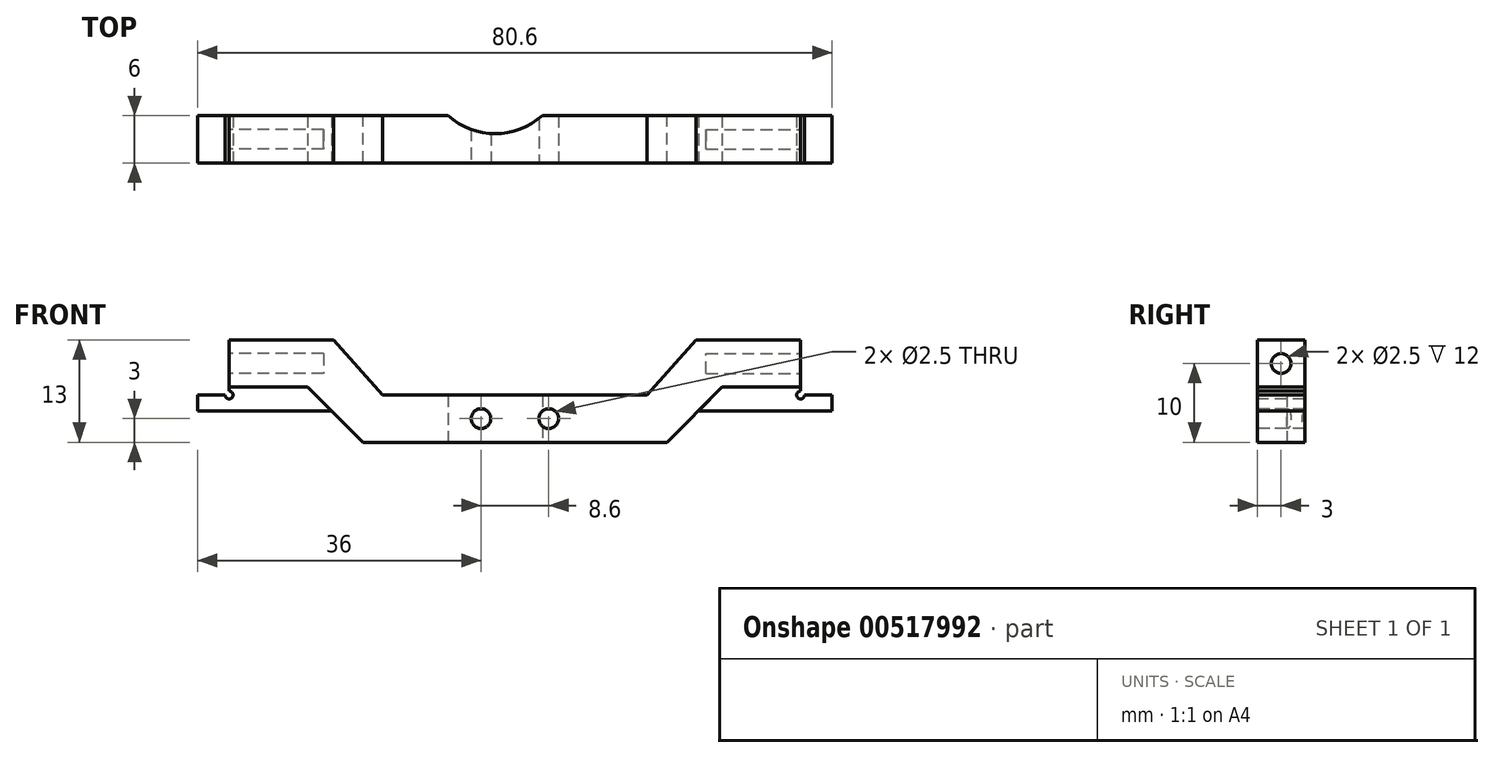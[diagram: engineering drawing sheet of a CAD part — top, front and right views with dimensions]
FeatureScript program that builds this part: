
annotation { "Feature Type Name" : "Feature", "Feature Type Description" : "" }
export const myFeature = defineFeature(function(context is Context, id is Id, definition is map)
    precondition{}
    {
        {
            var Q0;
            Q0=qCreatedBy(makeId("Top.planeOp"),FACE);
            var sketch = newSketch(context, id + "F0", { "sketchPlane" : qUnion([Q0])});
            skLineSegment(sketch, "E0.bottom", {"start": v(-33.8, 3) * mm, "end": v(38.8, 3) * mm});
            skLineSegment(sketch, "E0.top", {"start": v(-33.8, -3) * mm, "end": v(-6, -3) * mm});
            skLineSegment(sketch, "E0.left", {"start": v(-33.8, 3) * mm, "end": v(-33.8, -3) * mm});
            skLineSegment(sketch, "E0.right", {"start": v(38.8, 3) * mm, "end": v(38.8, -3) * mm});
            skLineSegment(sketch, "E1.trimOffspring", {"start": v(6, -3) * mm, "end": v(38.8, -3) * mm});
            skLineSegment(sketch, "E2", {"start": v(-6, -3) * mm, "end": v(6, -3) * mm});
            skSolve(sketch);
        }
        {
            var Q0;
            Q0=makeQuery(id+"F0.imprint","IMPRINT",FACE,{"disambiguationData":[TD([[makeQuery(id+"F0.imprint","IMPRINT",EDGE,{"derivedFrom":sQuery(id+"F0.wireOp",EDGE,"E0.bottom")}),-1.0]])]});
            extrude(context, id + "F1", {"entities" : qUnion([Q0]), "depth" : 13 * mm, "offsetDistance" : 25 * mm});
        }
        {
            var Q0;
            Q0=makeQuery(id+"F1.opExtrude","SWEPT_FACE",FACE,{"disambiguationData":[OSD([sQuery(id+"F0.wireOp",EDGE,"E0.bottom")])]});
            var sketch = newSketch(context, id + "F2", { "sketchPlane" : qUnion([Q0])});
            skLineSegment(sketch, "E3", {"start": v(-38.8, 0) * mm, "end": v(33.8, 0) * mm});
            skLineSegment(sketch, "E4", {"start": v(33.8, 0) * mm, "end": v(33.8, 13) * mm});
            skLineSegment(sketch, "E5", {"start": v(33.8, 13) * mm, "end": v(-38.8, 13) * mm});
            skLineSegment(sketch, "E6", {"start": v(-38.8, 13) * mm, "end": v(-38.8, 0) * mm});
            skLineSegment(sketch, "E7", {"start": v(-38.8, 7) * mm, "end": v(-28.8, 7) * mm});
            skLineSegment(sketch, "E8", {"start": v(-28.8, 7) * mm, "end": v(-28.8, 0) * mm});
            skLineSegment(sketch, "E9", {"start": v(23.8, 7) * mm, "end": v(23.8, 0) * mm});
            skLineSegment(sketch, "E10", {"start": v(-28.8, 7) * mm, "end": v(-21.8, 0) * mm});
            skLineSegment(sketch, "E11", {"start": v(23.8, 7) * mm, "end": v(16.8, 0) * mm});
            skLineSegment(sketch, "E12.trimOffspring", {"start": v(23.8, 7) * mm, "end": v(33.8, 7) * mm});
            skLineSegment(sketch, "E13.0", {"start": v(-24.56, 11.24) * mm, "end": v(-20.28, 6.97) * mm});
            skLineSegment(sketch, "E14.0", {"start": v(19.56, 11.24) * mm, "end": v(14.31, 6) * mm});
            skLineSegment(sketch, "E15", {"start": v(-19.31, 6) * mm, "end": v(14.31, 6) * mm});
            skPoint(sketch, "E15.startSnap0", {"position": v(-20.28, 6.97) * mm});
            skPoint(sketch, "E16.orphan", {"position": v(-27.25, 13.94) * mm});
            skPoint(sketch, "E17.orphan", {"position": v(-19.34, -2.46) * mm});
            skPoint(sketch, "E18.orphan", {"position": v(14.34, -2.46) * mm});
            skPoint(sketch, "E19.orphan", {"position": v(6.71, 0) * mm});
            skLineSegment(sketch, "E20.trimOffspring", {"start": v(-19.31, 6) * mm, "end": v(-25.51, 13) * mm});
            skPoint(sketch, "E21.end.orphan", {"position": v(-13.31, 0) * mm});
            skLineSegment(sketch, "E22.trimOffspring", {"start": v(14.31, 6) * mm, "end": v(20.51, 13) * mm});
            skPoint(sketch, "E23.orphan", {"position": v(-20.28, 6) * mm});
            skSolve(sketch);
        }
        {
            var Q0;
            {var subQ0=sQuery(id+"F2.wireOp",EDGE,"E8");Q0=makeQuery(id+"F2.imprint","IMPRINT",FACE,{"disambiguationData":[TD([[makeQuery(id+"F2.imprint","IMPRINT",EDGE,{"derivedFrom":subQ0}),1.0]])]});}
            var Q1;
            {var subQ4=sQuery(id+"F2.wireOp",EDGE,"E7");Q1=makeQuery(id+"F2.imprint","IMPRINT",FACE,{"disambiguationData":[TD([[makeQuery(id+"F2.imprint","IMPRINT",EDGE,{"derivedFrom":subQ4}),-1.0]])]});}
            var Q2;
            {var subQ3=sQuery(id+"F2.wireOp",EDGE,"E15");Q2=makeQuery(id+"F2.imprint","IMPRINT",FACE,{"disambiguationData":[TD([[makeQuery(id+"F2.imprint","IMPRINT",EDGE,{"derivedFrom":subQ3}),1.0]])]});}
            var Q3;
            {var subQ0=sQuery(id+"F2.wireOp",EDGE,"E9");Q3=makeQuery(id+"F2.imprint","IMPRINT",FACE,{"disambiguationData":[TD([[makeQuery(id+"F2.imprint","IMPRINT",EDGE,{"derivedFrom":subQ0}),-1.0]])]});}
            var Q4;
            {var subQ3=sQuery(id+"F2.wireOp",EDGE,"E9");Q4=makeQuery(id+"F2.imprint","IMPRINT",FACE,{"disambiguationData":[TD([[makeQuery(id+"F2.imprint","IMPRINT",EDGE,{"derivedFrom":subQ3}),1.0]])]});}
            extrude(context, id + "F3", {"entities" : qUnion([Q0, Q1, Q2, Q3, Q4]), "operationType" : NewBodyOperationType.REMOVE, "endBound" : BoundingType.THROUGH_ALL, "oppositeDirection" : true, "depth" : 25 * mm, "offsetDistance" : 25 * mm});
        }
        {
            var Q0;
            Q0=makeQuery(id+"F1.opExtrude","CAP_FACE",FACE,{"disambiguationData":[OSD([sQuery(id+"F0.wireOp",EDGE,"E0.bottom"),sQuery(id+"F0.wireOp",EDGE,"E0.top"),sQuery(id+"F0.wireOp",EDGE,"E0.left"),sQuery(id+"F0.wireOp",EDGE,"E0.right"),sQuery(id+"F0.wireOp",EDGE,"E1.trimOffspring"),sQuery(id+"F0.wireOp",EDGE,"E2")])],"isStart":true});
            var sketch = newSketch(context, id + "F4", { "sketchPlane" : qUnion([Q0])});
            skArc(sketch, "E24", {"start": v(6, -3) * mm, "mid": v(0, -0.7) * mm, "end": v(-6, -3) * mm});
            skSolve(sketch);
        }
        {
            var Q0;
            {var subQ0=sQuery(id+"F4.wireOp",EDGE,"E24");Q0=makeQuery(id+"F4.imprint","IMPRINT",FACE,{"disambiguationData":[TD([[makeQuery(id+"F4.imprint","IMPRINT",EDGE,{"derivedFrom":subQ0}),1.0]])]});}
            extrude(context, id + "F5", {"entities" : qUnion([Q0]), "operationType" : NewBodyOperationType.REMOVE, "endBound" : BoundingType.THROUGH_ALL, "oppositeDirection" : true, "depth" : 25 * mm, "offsetDistance" : 25 * mm});
        }
        {
            var Q0;
            Q0=makeQuery(id+"F1.opExtrude","SWEPT_FACE",FACE,{"disambiguationData":[OSD([sQuery(id+"F0.wireOp",EDGE,"E0.right")])]});
            var sketch = newSketch(context, id + "F6", { "sketchPlane" : qUnion([Q0])});
            skCircle(sketch, "E25", {"center": v(0, 10) * mm, "radius": 1.25 * mm});
            skSolve(sketch);
        }
        {
            var Q0;
            Q0=makeQuery(id+"F6.imprint","IMPRINT",FACE,{"disambiguationData":[TD([[makeQuery(id+"F6.imprint","IMPRINT",EDGE,{"derivedFrom":sQuery(id+"F6.wireOp",EDGE,"E25")}),1.0]])]});
            extrude(context, id + "F7", {"entities" : qUnion([Q0]), "operationType" : NewBodyOperationType.REMOVE, "oppositeDirection" : true, "depth" : 12 * mm, "offsetDistance" : 25 * mm});
        }
        {
            var Q0;
            Q0=makeQuery(id+"F1.opExtrude","SWEPT_FACE",FACE,{"disambiguationData":[OSD([sQuery(id+"F0.wireOp",EDGE,"E0.left")])]});
            var sketch = newSketch(context, id + "F8", { "sketchPlane" : qUnion([Q0])});
            skCircle(sketch, "E26", {"center": v(0, 10) * mm, "radius": 1.25 * mm});
            skSolve(sketch);
        }
        {
            var Q0;
            Q0=makeQuery(id+"F8.imprint","IMPRINT",FACE,{"disambiguationData":[TD([[makeQuery(id+"F8.imprint","IMPRINT",EDGE,{"derivedFrom":sQuery(id+"F8.wireOp",EDGE,"E26")}),1.0]])]});
            extrude(context, id + "F9", {"entities" : qUnion([Q0]), "operationType" : NewBodyOperationType.REMOVE, "oppositeDirection" : true, "depth" : 12 * mm, "offsetDistance" : 25 * mm});
        }
        {
            var Q0;
            Q0=makeQuery(id+"F1.opExtrude","SWEPT_FACE",FACE,{"disambiguationData":[OSD([sQuery(id+"F0.wireOp",EDGE,"E0.top"),sQuery(id+"F0.wireOp",EDGE,"E1.trimOffspring"),sQuery(id+"F0.wireOp",EDGE,"E2")])]});
            var sketch = newSketch(context, id + "F10", { "sketchPlane" : qUnion([Q0])});
            skCircle(sketch, "E27", {"center": v(-1.8, 3) * mm, "radius": 1.25 * mm});
            skCircle(sketch, "E28", {"center": v(6.8, 3) * mm, "radius": 1.25 * mm});
            skSolve(sketch);
        }
        {
            var Q0;
            Q0=makeQuery(id+"F10.imprint","IMPRINT",FACE,{"disambiguationData":[TD([[makeQuery(id+"F10.imprint","IMPRINT",EDGE,{"derivedFrom":sQuery(id+"F10.wireOp",EDGE,"E27")}),1.0]])]});
            var Q1;
            Q1=makeQuery(id+"F10.imprint","IMPRINT",FACE,{"disambiguationData":[TD([[makeQuery(id+"F10.imprint","IMPRINT",EDGE,{"derivedFrom":sQuery(id+"F10.wireOp",EDGE,"E28")}),1.0]])]});
            extrude(context, id + "F11", {"entities" : qUnion([Q0, Q1]), "operationType" : NewBodyOperationType.REMOVE, "endBound" : BoundingType.THROUGH_ALL, "oppositeDirection" : true, "depth" : 25 * mm, "offsetDistance" : 25 * mm});
        }
        {
            var Q0;
            Q0=makeQuery(id+"F1.opExtrude","SWEPT_FACE",FACE,{"disambiguationData":[OSD([sQuery(id+"F0.wireOp",EDGE,"E0.top"),sQuery(id+"F0.wireOp",EDGE,"E1.trimOffspring"),sQuery(id+"F0.wireOp",EDGE,"E2")])]});
            var sketch = newSketch(context, id + "F12", { "sketchPlane" : qUnion([Q0])});
            skLineSegment(sketch, "E29", {"start": v(38.8, 7) * mm, "end": v(38.8, 6.5) * mm});
            skLineSegment(sketch, "E30", {"start": v(39.3, 6) * mm, "end": v(42.8, 6) * mm});
            skLineSegment(sketch, "E31", {"start": v(42.8, 6) * mm, "end": v(42.8, 4) * mm});
            skLineSegment(sketch, "E32", {"start": v(42.8, 4) * mm, "end": v(25.8, 4) * mm});
            skArc(sketch, "E33", {"start": v(38.8, 6.5) * mm, "mid": v(38.45, 5.65) * mm, "end": v(39.3, 6) * mm});
            skLineSegment(sketch, "E34", {"start": v(-33.8, 7) * mm, "end": v(-33.8, 6.5) * mm});
            skLineSegment(sketch, "E35", {"start": v(-34.3, 6) * mm, "end": v(-37.8, 6) * mm});
            skLineSegment(sketch, "E36", {"start": v(-37.8, 6) * mm, "end": v(-37.8, 4) * mm});
            skLineSegment(sketch, "E37", {"start": v(-37.8, 4) * mm, "end": v(-20.8, 4) * mm});
            skArc(sketch, "E38", {"start": v(-34.3, 6) * mm, "mid": v(-33.45, 5.65) * mm, "end": v(-33.8, 6.5) * mm});
            skSolve(sketch);
        }
        {
            var Q0;
            Q0=makeQuery(id+"F12.imprint","IMPRINT",FACE,{"disambiguationData":[TD([[makeQuery(id+"F12.imprint","IMPRINT",EDGE,{"derivedFrom":sQuery(id+"F12.wireOp",EDGE,"E29")}),-1.0]])]});
            var Q1;
            Q1=makeQuery(id+"F12.imprint","IMPRINT",FACE,{"disambiguationData":[TD([[makeQuery(id+"F12.imprint","IMPRINT",EDGE,{"derivedFrom":sQuery(id+"F12.wireOp",EDGE,"E34")}),1.0]])]});
            extrude(context, id + "F13", {"entities" : qUnion([Q0, Q1]), "oppositeDirection" : true, "depth" : 6 * mm, "offsetDistance" : 25 * mm});
        }
    });
